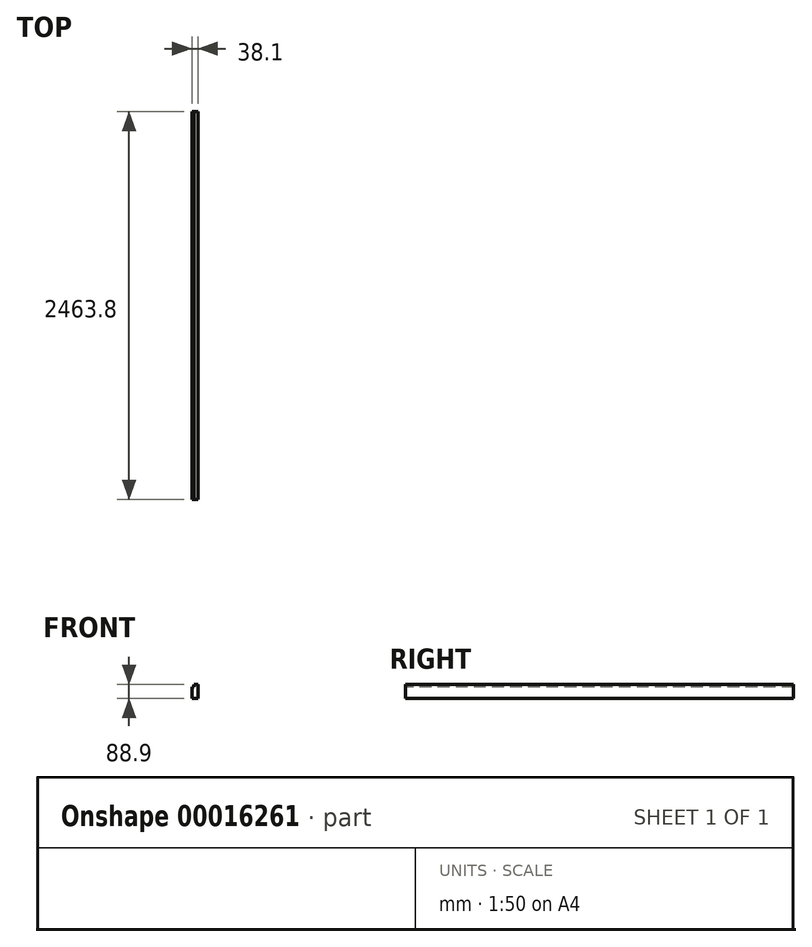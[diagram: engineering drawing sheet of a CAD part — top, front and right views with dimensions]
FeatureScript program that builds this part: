
annotation { "Feature Type Name" : "Feature", "Feature Type Description" : "" }
export const myFeature = defineFeature(function(context is Context, id is Id, definition is map)
    precondition{}
    {
        {
            var Q0;
            Q0=qCreatedBy(makeId("Front.planeOp"),FACE);
            var sketch = newSketch(context, id + "F0", { "sketchPlane" : qUnion([Q0])});
            skLineSegment(sketch, "E0.bottom", {"start": v(0, 0) * mm, "end": v(-38.1, 0) * mm});
            skLineSegment(sketch, "E0.left", {"start": v(0, 0) * mm, "end": v(0, 88.9) * mm});
            skLineSegment(sketch, "E0.right", {"start": v(-38.1, 0) * mm, "end": v(-38.1, 73.03) * mm});
            skLineSegment(sketch, "E1.top", {"start": v(0, 88.9) * mm, "end": v(-25.4, 88.9) * mm});
            skLineSegment(sketch, "E1.right", {"start": v(-25.4, 73.03) * mm, "end": v(-25.4, 88.9) * mm});
            skLineSegment(sketch, "E2", {"start": v(-38.1, 73.03) * mm, "end": v(-25.4, 73.03) * mm});
            skSolve(sketch);
        }
        {
            var Q0;
            Q0=makeQuery(id+"F0.imprint","IMPRINT",FACE,{"disambiguationData":[TD([[makeQuery(id+"F0.imprint","IMPRINT",EDGE,{"derivedFrom":sQuery(id+"F0.wireOp",EDGE,"E0.bottom")}),-1.0]])]});
            extrude(context, id + "F1", {"entities" : qUnion([Q0]), "oppositeDirection" : true, "depth" : 2463.8 * mm});
        }
    });
